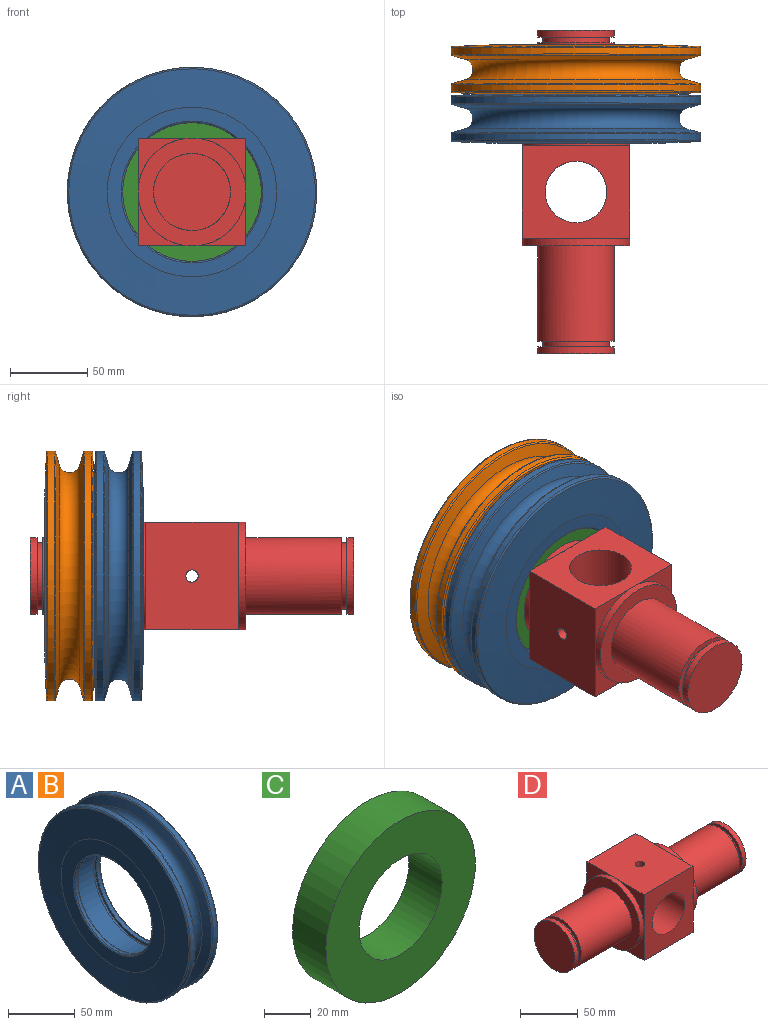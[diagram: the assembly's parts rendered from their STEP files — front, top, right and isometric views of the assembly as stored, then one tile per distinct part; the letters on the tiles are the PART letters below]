
ASSEMBLY  parts=4 mates=4
PART A: 23 faces, bbox 32x175.3x175.3 mm
  f0: plane 110x110mm, normal (-1,0,0), area 3961.5mm2, adj f1,f22
  f1: torus R=42mm, axis (-1,0,0), area 408.2mm2, adj f0,f2
  f2: cylinder r=41mm len=82mm, axis (-1,0,0), area 644mm2, adj f1,f3
  f3: torus R=42mm, axis (-1,0,0), area 408.2mm2, adj f2,f4
  f4: plane 90x90mm, normal (1,0,0), area 820mm2, adj f3,f5
  f5: cylinder r=45mm len=90mm, axis (-1,0,0), area 5654.9mm2, adj f4,f6
  f6: plane 94x94mm, normal (1,0,0), area 578.1mm2, adj f5,f7
  f7: cylinder r=47mm len=94mm, axis (-1,0,0), area 930.2mm2, adj f6,f8
  f8: plane 94x94mm, normal (-1,0,0), area 578.1mm2, adj f7,f9
  f9: cylinder r=45mm len=90mm, axis (-1,0,0), area 947.2mm2, adj f8,f10
  f10: torus R=46mm, axis (-1,0,0), area 447.7mm2, adj f9,f11
  f11: plane 110x110mm, normal (1,0,0), area 2855.7mm2, adj f10,f12
  f12: cone r=55mm half-angle=87.7deg, axis (-1,0,0), area 10611.4mm2, adj f11,f13
  f13: torus R=79.96mm, axis (-1,0,0), area 775.4mm2, adj f12,f14
  f14: cylinder r=80.96mm len=161.92mm, axis (-1,0,0), area 2054.7mm2, adj f13,f15
  f15: torus R=79.96mm, axis (-1,0,0), area 659.6mm2, adj f14,f16
  f16: cone r=72.09mm half-angle=74.5deg, axis (1,0,0), area 4038.8mm2, adj f15,f17
  f17: torus R=73.96mm, axis (-1,0,0), area 7869.1mm2, adj f16,f18
  f18: cone r=80.23mm half-angle=74.5deg, axis (-1,0,0), area 4038.8mm2, adj f17,f19
  f19: torus R=79.96mm, axis (-1,0,0), area 659.6mm2, adj f18,f20
  f20: cylinder r=80.96mm len=161.92mm, axis (-1,0,0), area 2054.7mm2, adj f19,f21
  f21: torus R=79.96mm, axis (-1,0,0), area 775.4mm2, adj f20,f22
  f22: cone r=55mm half-angle=87.7deg, axis (1,0,0), area 10611.4mm2, adj f0,f21
PART B: same geometry as A
PART C: 4 faces, bbox 90x20x90 mm
  f0: cylinder r=45mm len=90mm, axis (0,1,0), area 5654.9mm2, adj f2,f3
  f1: cylinder r=25mm len=50mm, axis (0,1,0), area 3141.6mm2, adj f2,f3
  f2: plane 90x90mm, normal (0,-1,0), area 4398.2mm2, adj f0,f1
  f3: plane 90x90mm, normal (0,1,0), area 4398.2mm2, adj f0,f1
PART D: 31 faces, bbox 210x70x70 mm
  f0: plane 35x35mm, normal (-1,0,0), area 262.9mm2, adj f7,f10,f17
  f1: plane 35x35mm, normal (-1,0,0), area 262.9mm2, adj f9,f10,f17
  f2: plane 35x35mm, normal (-1,0,0), area 262.9mm2, adj f8,f9,f17
  f3: plane 35x35mm, normal (-1,0,0), area 262.9mm2, adj f7,f8,f17
  f4: plane 35x35mm, normal (1,0,0), area 262.9mm2, adj f9,f10,f13
  f5: plane 35x35mm, normal (1,0,0), area 262.9mm2, adj f7,f10,f13
  f6: plane 35x35mm, normal (1,0,0), area 262.9mm2, adj f7,f8,f13
  f7: plane 70x60mm, normal (0,0,1), area 4149.7mm2, adj f0,f3,f5,f6,f8,f10,f30
  f8: plane 70x60mm, normal (0,-1,0), area 2943.4mm2, adj f2,f3,f6,f7,f9,f11,f12
  f9: plane 70x60mm, normal (0,0,-1), area 4149.7mm2, adj f1,f2,f4,f8,f10,f11,f29
  f10: plane 70x60mm, normal (0,1,0), area 2943.4mm2, adj f0,f1,f4,f5,f7,f9,f12
  f11: plane 35x35mm, normal (1,0,0), area 262.9mm2, adj f8,f9,f13
  f12: cylinder r=20mm len=70mm, axis (0,1,0), area 8695.3mm2, adj f8,f10,f29,f30
  f13: cylinder r=35mm len=70mm, axis (-1,0,0), area 1099.6mm2, adj f4,f5,f6,f11,f14
  f14: plane 70x70mm, normal (1,0,0), area 1885mm2, adj f13,f16
  f15: plane 50x50mm, normal (1,0,0), area 511.3mm2, adj f16,f25
  f16: cylinder r=25mm len=62mm, axis (1,0,0), area 9738.9mm2, adj f14,f15
  f17: cylinder r=35mm len=70mm, axis (1,0,0), area 1099.6mm2, adj f0,f1,f2,f3,f18
  f18: plane 70x70mm, normal (-1,0,0), area 1885mm2, adj f17,f20
  f19: plane 50x50mm, normal (-1,0,0), area 511.3mm2, adj f20,f21
  f20: cylinder r=25mm len=62mm, axis (1,0,0), area 9738.9mm2, adj f18,f19
  f21: cylinder r=21.5mm len=43mm, axis (1,0,0), area 472.8mm2, adj f19,f24
  f22: cylinder r=24.95mm len=49.9mm, axis (1,0,0), area 705.4mm2, adj f23,f24
  f23: plane 49.9x49.9mm, normal (-1,0,0), area 1955.6mm2, adj f22
  f24: plane 49.9x49.9mm, normal (1,0,0), area 503.4mm2, adj f21,f22
  f25: cylinder r=21.5mm len=43mm, axis (-1,0,0), area 472.8mm2, adj f15,f28
  f26: cylinder r=24.95mm len=49.9mm, axis (-1,0,0), area 705.4mm2, adj f27,f28
  f27: plane 49.9x49.9mm, normal (1,0,0), area 1955.6mm2, adj f26
  f28: plane 49.9x49.9mm, normal (-1,0,0), area 503.4mm2, adj f25,f26
  f29: cylinder r=4mm len=15.4mm, axis (0,0,1), area 382.1mm2, adj f9,f12
  f30: cylinder r=4mm len=15.4mm, axis (0,0,1), area 382.1mm2, adj f7,f12
PLACE A rot(axis=(0.58,-0.58,-0.58),120deg) t=(-70.61,6.03,29.68)mm
PLACE B rot(axis=(0,0,1),90deg) t=(-70.61,37.83,29.68)mm
PLACE C rot(axis=(0,-1,0),180deg) t=(-70.61,8.66,29.68)mm
PLACE D rot(axis=(-0.58,-0.58,0.58),120deg) t=(-70.61,-41.63,29.68)mm
MATE parallel C.f0 <-> D.f13  axis (0,-1,0) through (-70.61,-1.34,29.68)mm
MATE slider D.f16 <-> C.f1  axis (0,1,0) through (-70.61,24.37,29.68)mm
MATE slider C.f0 <-> A.f1  axis (0,1,0) through (-70.61,8.66,29.68)mm
MATE slider B.f1 <-> D.f16  axis (0,-1,0) through (-70.61,36.33,29.68)mm
